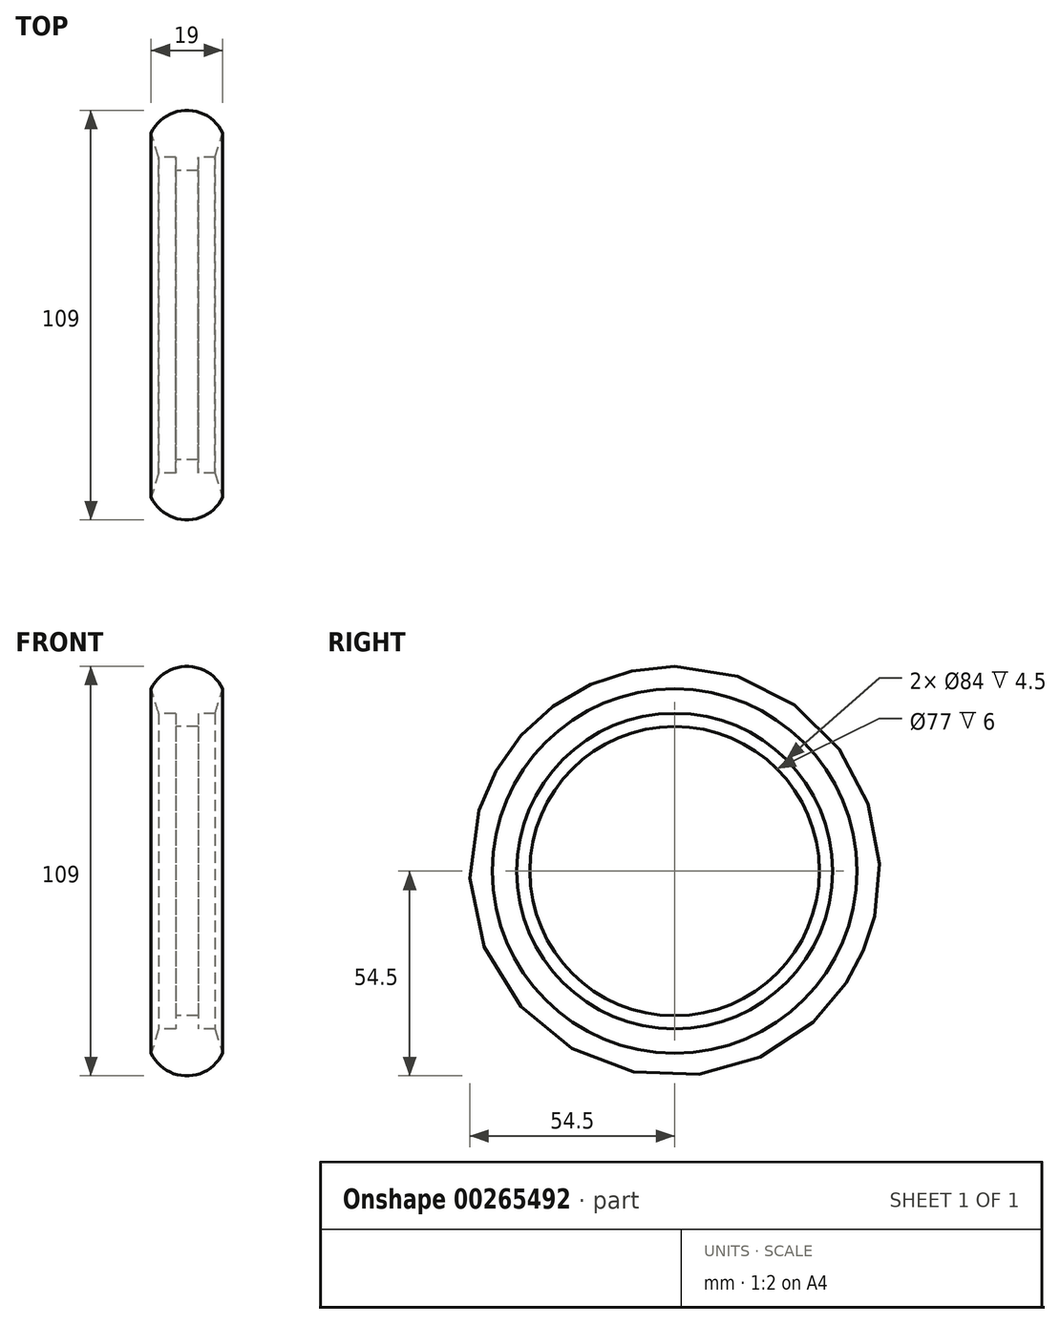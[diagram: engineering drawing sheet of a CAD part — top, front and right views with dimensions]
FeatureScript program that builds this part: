
annotation { "Feature Type Name" : "Feature", "Feature Type Description" : "" }
export const myFeature = defineFeature(function(context is Context, id is Id, definition is map)
    precondition{}
    {
        {
            var Q0;
            Q0=qCreatedBy(makeId("Front.planeOp"),FACE);
            var sketch = newSketch(context, id + "F0", { "sketchPlane" : qUnion([Q0])});
            skLineSegment(sketch, "E0", {"start": v(0, 0) * mm, "end": v(0, 54.5) * mm, "construction": true});
            skLineSegment(sketch, "E1", {"start": v(0, 54.5) * mm, "end": v(0, 38.5) * mm, "construction": true});
            skLineSegment(sketch, "E2", {"start": v(0, 38.5) * mm, "end": v(-3, 38.5) * mm});
            skLineSegment(sketch, "E3", {"start": v(-3, 38.5) * mm, "end": v(-3, 42) * mm});
            skLineSegment(sketch, "E4", {"start": v(-3, 42) * mm, "end": v(-7.5, 42) * mm});
            skLineSegment(sketch, "E5", {"start": v(-7.5, 42) * mm, "end": v(-7.5, 48.5) * mm, "construction": true});
            skLineSegment(sketch, "E6", {"start": v(-7.5, 48.5) * mm, "end": v(-9.5, 48.5) * mm, "construction": true});
            skLineSegment(sketch, "E7", {"start": v(-9.5, 48.5) * mm, "end": v(-7.5, 42) * mm});
            skArc(sketch, "E8", {"start": v(0, 54.5) * mm, "mid": v(-5.62, 52.87) * mm, "end": v(-9.5, 48.5) * mm});
            skArc(sketch, "E9.MirrorCS", {"start": v(0, 54.5) * mm, "mid": v(5.62, 52.87) * mm, "end": v(9.5, 48.5) * mm});
            skLineSegment(sketch, "E10.MirrorCS", {"start": v(9.5, 48.5) * mm, "end": v(7.5, 42) * mm});
            skLineSegment(sketch, "E11.MirrorCS", {"start": v(3, 42) * mm, "end": v(7.5, 42) * mm});
            skLineSegment(sketch, "E12.MirrorCS", {"start": v(3, 38.5) * mm, "end": v(3, 42) * mm});
            skLineSegment(sketch, "E13.MirrorCS", {"start": v(0, 38.5) * mm, "end": v(3, 38.5) * mm});
            skLineSegment(sketch, "E14", {"start": v(0, 0) * mm, "end": v(-28.58, 0) * mm, "construction": true});
            skLineSegment(sketch, "E15", {"start": v(-28.58, 0) * mm, "end": v(30.86, 0) * mm, "construction": true});
            skSolve(sketch);
        }
        {
            var Q0;
            Q0=makeQuery(id+"F0.imprint","IMPRINT",FACE,{"disambiguationData":[TD([[makeQuery(id+"F0.imprint","IMPRINT",EDGE,{"derivedFrom":sQuery(id+"F0.wireOp",EDGE,"E2")}),-1.0]])]});
            var Q1;
            Q1=sQuery(id+"F0.wireOp",EDGE,"E15");
            revolve(context, id + "F1", {"entities" : qUnion([Q0]), "axis" : qUnion([Q1]), "revolveType" : RevolveType.FULL});
        }
    });
